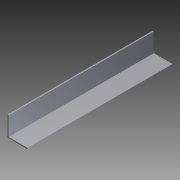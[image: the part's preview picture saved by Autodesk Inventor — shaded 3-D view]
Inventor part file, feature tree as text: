
AUTODESK INVENTOR PART (.ipt)
format: ipt  version: 2012 (Build 160160000, 160)  size: 74,752 bytes
history: native  units: in
note: dims shown in document units (in); Inventor stores cm internally (conversion verified against a paired STEP export)
features: extrude x1, sketch x1
ambient origin geometry x8: Origin, YZ Plane, XZ Plane, XY Plane, X Axis, Y Axis, Z Axis, Center Point
bodies: Solid1 (feature_tree)
feature tree (2):
  extrude  "Extrusion1"  Depth=0.0625in
  sketch  "Sketch1"  dims[d0=0.0625in d1=0.0625in d2=1.0in d3=1.0in d4=7.25in d5=0.0in]
